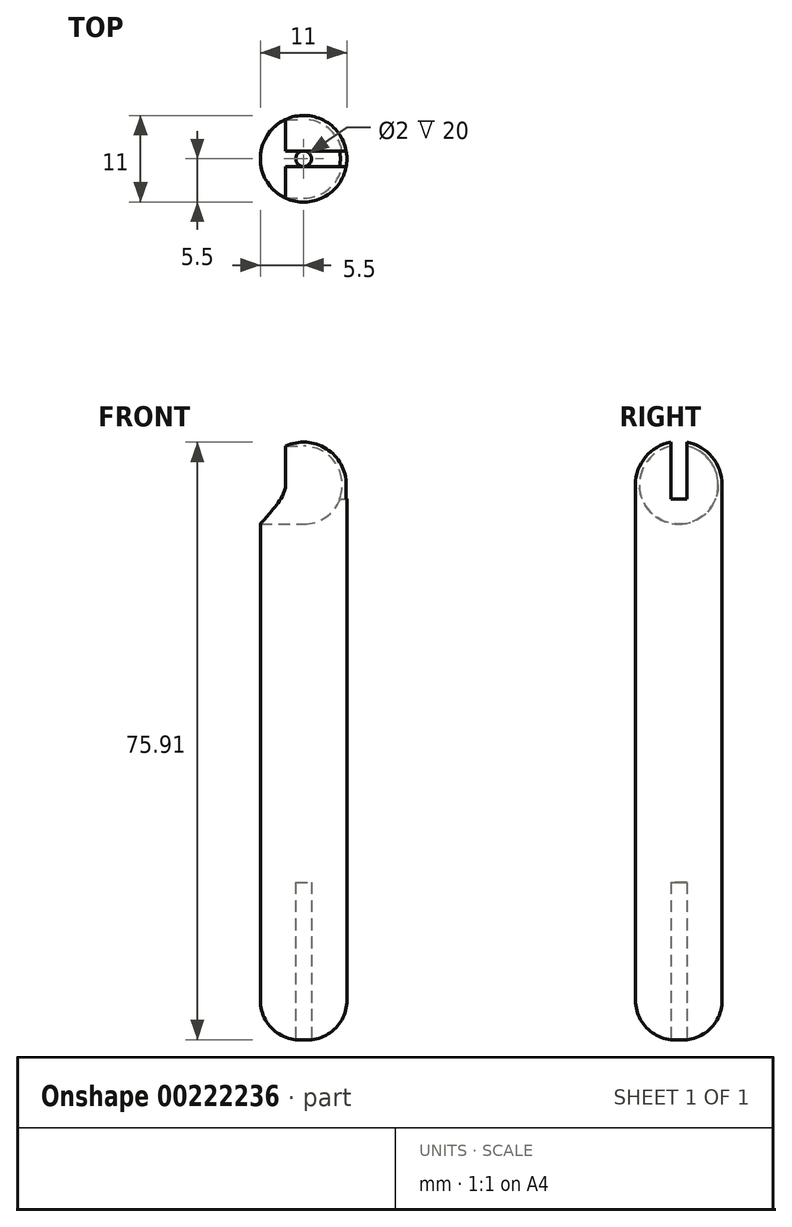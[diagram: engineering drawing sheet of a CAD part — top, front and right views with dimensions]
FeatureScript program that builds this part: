
annotation { "Feature Type Name" : "Feature", "Feature Type Description" : "" }
export const myFeature = defineFeature(function(context is Context, id is Id, definition is map)
    precondition{}
    {
        {
            var Q0;
            Q0=qCreatedBy(makeId("Front.planeOp"),FACE);
            var sketch = newSketch(context, id + "F0", { "sketchPlane" : qUnion([Q0])});
            skCircle(sketch, "E0", {"center": v(0, 0) * mm, "radius": 5.5 * mm});
            skCircle(sketch, "E1", {"center": v(0, 0) * mm, "radius": 5 * mm});
            skLineSegment(sketch, "E2", {"start": v(0, 5.5) * mm, "end": v(0, -70.5) * mm});
            skPoint(sketch, "E3", {"position": v(0, 5) * mm});
            skPoint(sketch, "E4", {"position": v(0, -5) * mm});
            skPoint(sketch, "E5", {"position": v(0, -5.5) * mm});
            skPoint(sketch, "E6", {"position": v(-5.5, 0) * mm});
            skPoint(sketch, "E7", {"position": v(-5.5, -70.5) * mm});
            skLineSegment(sketch, "E8", {"start": v(-5.5, 0) * mm, "end": v(-5.5, -70.5) * mm});
            skLineSegment(sketch, "E9", {"start": v(-5.5, -70.5) * mm, "end": v(0, -70.5) * mm});
            skSolve(sketch);
        }
        {
            var Q0;
            {var subQ0=sQuery(id+"F0.wireOp",EDGE,"E2");var subQ4=sQuery(id+"F0.wireOp",EDGE,"E0");var subQ7=makeQuery(id+"F0.imprint","INTERSECT",VERTEX,{"disambiguationData":[OD(0.0)],"derivedFrom":[subQ4,subQ0]});Q0=makeQuery(id+"F0.imprint","IMPRINT",FACE,{"disambiguationData":[TD([[makeQuery(id+"F0.imprint","IMPRINT",EDGE,{"disambiguationData":[TD([[subQ7,-1.0]])],"derivedFrom":subQ4}),1.0]])]});}
            var Q1;
            {var subQ0=sQuery(id+"F0.wireOp",EDGE,"E8");Q1=makeQuery(id+"F0.imprint","IMPRINT",FACE,{"disambiguationData":[TD([[makeQuery(id+"F0.imprint","IMPRINT",EDGE,{"derivedFrom":subQ0}),1.0]])]});}
            var Q2;
            Q2=sQuery(id+"F0.wireOp",EDGE,"E2");
            revolve(context, id + "F1", {"surfaceOperationType" : NewSurfaceOperationType.NEW, "entities" : qUnion([Q0, Q1]), "axis" : qUnion([Q2]), "revolveType" : RevolveType.FULL});
        }
        {
            var Q0;
            Q0=qCreatedBy(makeId("Right.planeOp"),FACE);
            var sketch = newSketch(context, id + "F2", { "sketchPlane" : qUnion([Q0])});
            skPoint(sketch, "E10", {"position": v(0, 0) * mm});
            skCircle(sketch, "E11", {"center": v(0, 0) * mm, "radius": 5 * mm});
            skSolve(sketch);
        }
        {
            var Q0;
            Q0 = qSketchRegion(id + "F2", true);
            extrude(context, id + "F3", {"entities" : qUnion([Q0]), "operationType" : NewBodyOperationType.REMOVE, "endBound" : BoundingType.THROUGH_ALL, "oppositeDirection" : true, "depth" : 10 * mm, "offsetDistance" : 25 * mm});
        }
        {
            var Q0;
            Q0=qCreatedBy(makeId("Right.planeOp"),FACE);
            var sketch = newSketch(context, id + "F4", { "sketchPlane" : qUnion([Q0])});
            skPoint(sketch, "E12", {"position": v(0, 0) * mm});
            skPoint(sketch, "E13", {"position": v(0, 2.7) * mm});
            skLineSegment(sketch, "E14.bottom", {"start": v(-1, 7.2) * mm, "end": v(1, 7.2) * mm});
            skLineSegment(sketch, "E14.top", {"start": v(-1, -1.8) * mm, "end": v(1, -1.8) * mm});
            skLineSegment(sketch, "E14.left", {"start": v(-1, 7.2) * mm, "end": v(-1, -1.8) * mm});
            skLineSegment(sketch, "E14.right", {"start": v(1, 7.2) * mm, "end": v(1, -1.8) * mm});
            skSolve(sketch);
        }
        {
            var Q0;
            Q0=makeQuery(id+"F4.imprint","IMPRINT",FACE,{"disambiguationData":[TD([[makeQuery(id+"F4.imprint","IMPRINT",EDGE,{"derivedFrom":sQuery(id+"F4.wireOp",EDGE,"E14.bottom")}),-1.0]])]});
            extrude(context, id + "F5", {"entities" : qUnion([Q0]), "operationType" : NewBodyOperationType.REMOVE, "oppositeDirection" : true, "depth" : 12 * mm, "offsetDistance" : 25 * mm, "hasSecondDirection" : true, "secondDirectionOppositeDirection" : false, "secondDirectionDepth" : 25 * mm});
        }
        {
            var Q0;
            Q0=makeQuery(id+"F1.opRevolve","SWEPT_FACE",FACE,{"disambiguationData":[OSD([sQuery(id+"F0.wireOp",EDGE,"E9")])]});
            var sketch = newSketch(context, id + "F6", { "sketchPlane" : qUnion([Q0])});
            skPoint(sketch, "E15", {"position": v(0, 0) * mm});
            skCircle(sketch, "E16", {"center": v(0, 0) * mm, "radius": 1 * mm});
            skSolve(sketch);
        }
        {
            var Q0;
            Q0=makeQuery(id+"F6.imprint","IMPRINT",FACE,{"disambiguationData":[TD([[makeQuery(id+"F6.imprint","IMPRINT",EDGE,{"derivedFrom":sQuery(id+"F6.wireOp",EDGE,"E16")}),1.0]])]});
            extrude(context, id + "F7", {"entities" : qUnion([Q0]), "operationType" : NewBodyOperationType.REMOVE, "oppositeDirection" : true, "depth" : 20 * mm, "offsetDistance" : 25 * mm});
        }
        {
            var Q0;
            Q0=makeQuery(id+"F1.opRevolve","SWEPT_EDGE",EDGE,{"disambiguationData":[OSD([sQuery(id+"F0.wireOp",EDGE,"E8"),sQuery(id+"F0.wireOp",EDGE,"E9")])]});
            fillet(context, id + "F8", {"entities" : qUnion([Q0]), "radius" : 5 * mm, "tangentPropagation" : true, "allowEdgeOverflow" : false});
        }
    });
